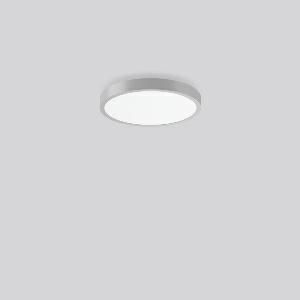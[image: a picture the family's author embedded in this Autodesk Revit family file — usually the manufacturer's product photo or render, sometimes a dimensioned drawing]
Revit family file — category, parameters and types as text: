
# Revit family: triona_round_a_312419_004_2_730_e5a6
name_source: partatom
category: Lighting Fixtures
units: mm (PartAtom-declared; Revit-internal decimal feet)

## family parameters
Cut with Voids When Loaded = No
Host = Face
Light Source = No
Part Type = Normal
Room Calculation Point = No
Round Connector Dimension = Use Diameter
Shared = No

## types (1)
- TuneableWhite 846 (1 x LED Modul 846, 2450 lm, 4600)
    Apparent Load = 29 VA
    CIE Flux Codes = 48 80 96 100 100
    Color Rendering = 80
    Color Temperature = 4600
    Default Elevation = 1800 mm
    Description = Series: TRIONA round
Decorative round LED surface-mounted luminaire. Flat, seamless frame: aluminium extrusion profile, powder coated. Cover made of sheet steel, powder-coated. Light emission through a diffuser: plastic, opal. Lightguide and diffuser made of non-yellowing plastic (PMMA). Lateral light emission (RZB SIDELITE technology) for above-average homogeneous light distribution. Tunable white versions, dynamically adjustable from 2700 K to 6500 K. Suitable for Ceiling mounting, Wall (surface). Tool-free mounting via bayonet connection. Electronic ballast included. Very easy installation thanks to Plug+Play connection. With Casambi smart+free Bluetooth control for wireless network and operation using Android / iOS devices, free app available for download. Ideal for use as part of the Human Centric Lighting concept in connection with RZB light management systems. 
Colour: silver, matt (approx. RAL 9006)
Diameter: 461 mm
Height: 88 mm
Lamp: LED
Socket: without socket
Colour temperature: 2700K - 6500K
Colour rendering index (CRI): 80
System power: 29 W
Rated luminous flux: 2450 lm
Luminous efficiency: 84 lm/W
System power 2: 29 W
Rated luminous flux 2: 2350 lm
Luminous efficiency 2: 81 lm/W
System power 3: 30 W
Rated luminous flux 3: 2400 lm
Luminous efficiency 3: 80 lm/W
Control gear: Dimmable Bluetooth converter
Protection class: I
Type of protection: IP 20
    Height = 88 mm
    Lamp = 1 x LED Modul 846
    Lamp Light Flux = 2450 lm
    Lamp count = 1
    Length = 461 mm
    Lifetime = 50000 h
    Luminous efficacy = 84 lm/W
    Manufacturer = RZB
    ModVariant = No
    Model = 312419.004.2.730
    Mounting Place = Ceiling
    Mounting Type = Surface mounted
    Number of Poles = 1
    OnlyDefault = Yes
    Power Factor = 1
    Product Name = TRIONA round A
    Product group = Surface mounted modular luminaires
    ProductGroupID = 306
    Protection Class = Protection class I
    Protection Degree = IP 20
    RLX_Detail_Level = 1
    RLX_Emergency_Light_Flux = 0 lm
    RLX_Emergency_Type = 0
    RLX_Emergency_Type_DB = No
    RlxData = <blob elided: 28709 chars, md5=8b1c7018>
    Socket = socket
    Standby Power = 0 W
    System Light Flux = 2450 lm
    System Power = 29 W
    Type Comments = TuneableWhite 846
    Type Image = 312420.004.jpg
    URL = http://relux.com
    VarID = tuneablewhite_846
    Voltage = 230 V
    Voltage Range = 220-240 V
    Weight = 0.00 kg
    Width = 0 mm  [stored 0 ft]

note: [stored X ft] marks values corroborated as IEEE doubles in the binary element streams (Revit-internal decimal feet)

## geometry (parser evidence)
native form markers: Blend x4, Sweep x10
no freeform markers — native parametric forms only
